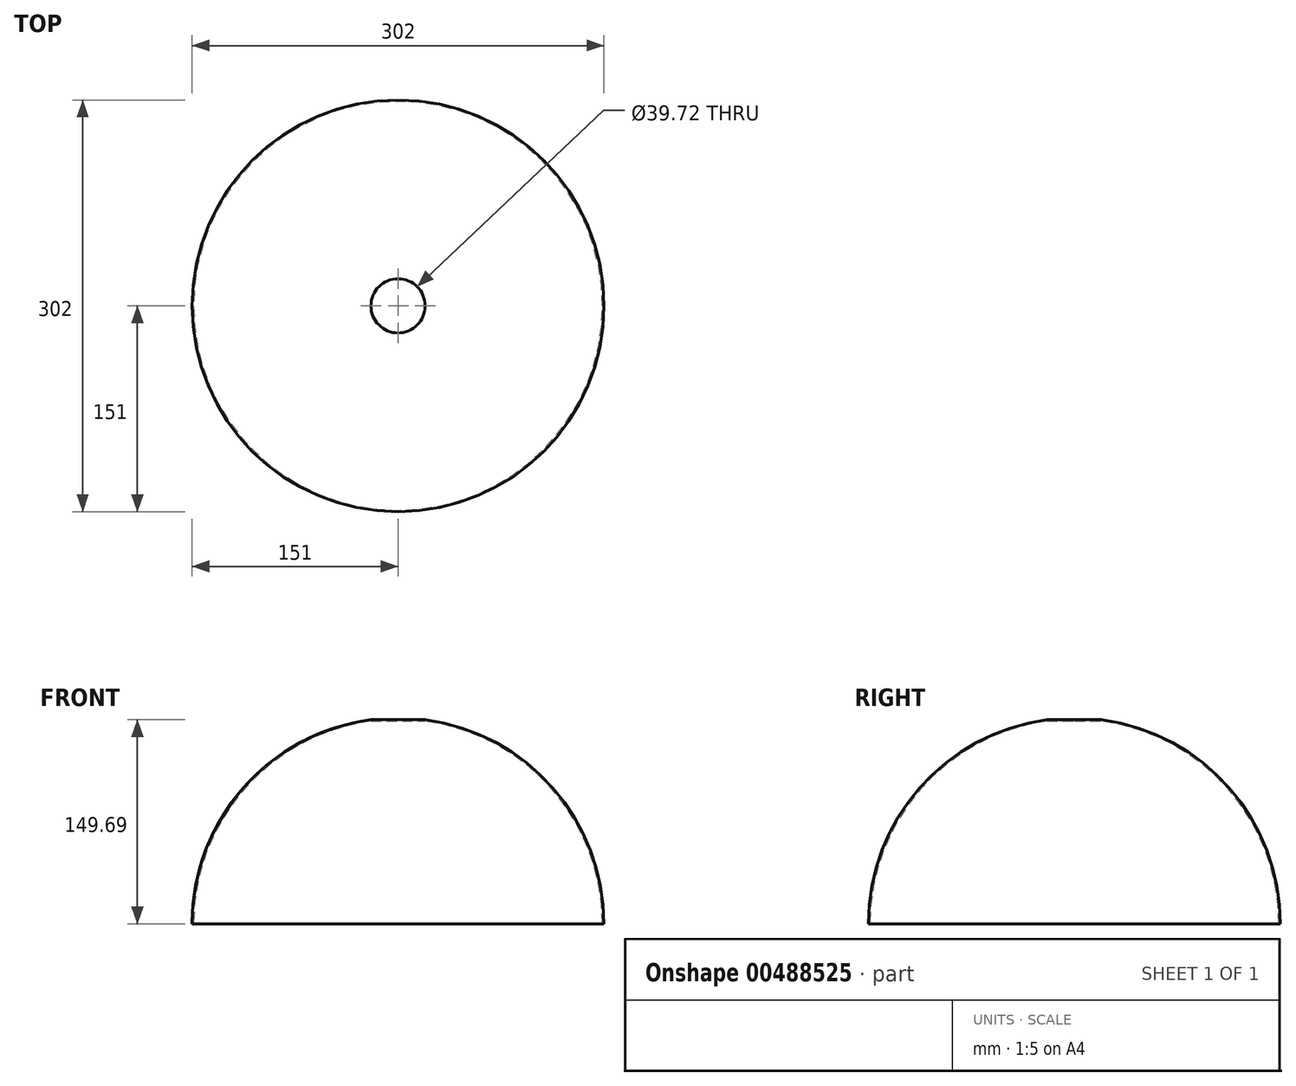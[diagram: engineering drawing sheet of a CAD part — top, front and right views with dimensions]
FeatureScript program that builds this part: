
annotation { "Feature Type Name" : "Feature", "Feature Type Description" : "" }
export const myFeature = defineFeature(function(context is Context, id is Id, definition is map)
    precondition{}
    {
        {
            var Q0;
            Q0=qCreatedBy(makeId("Front.planeOp"),FACE);
            var sketch = newSketch(context, id + "F0", { "sketchPlane" : qUnion([Q0])});
            skArc(sketch, "E0", {"start": v(150, 0) * mm, "mid": v(112.87, 98.8) * mm, "end": v(19.86, 148.68) * mm});
            skArc(sketch, "E1.0", {"start": v(151, 0) * mm, "mid": v(113.58, 99.5) * mm, "end": v(19.86, 149.69) * mm});
            skLineSegment(sketch, "E2", {"start": v(0, 0) * mm, "end": v(0, 150) * mm});
            skLineSegment(sketch, "E3", {"start": v(150, 0) * mm, "end": v(151, 0) * mm});
            skLineSegment(sketch, "E4", {"start": v(19.86, 149.69) * mm, "end": v(19.86, 148.68) * mm});
            skSolve(sketch);
        }
        {
            var Q0;
            Q0=makeQuery(id+"F0.imprint","IMPRINT",FACE,{"disambiguationData":[TD([[makeQuery(id+"F0.imprint","IMPRINT",EDGE,{"derivedFrom":sQuery(id+"F0.wireOp",EDGE,"E0")}),-1.0]])]});
            var Q1;
            Q1=sQuery(id+"F0.wireOp",EDGE,"E2");
            revolve(context, id + "F1", {"entities" : qUnion([Q0]), "axis" : qUnion([Q1]), "revolveType" : RevolveType.FULL});
        }
    });
